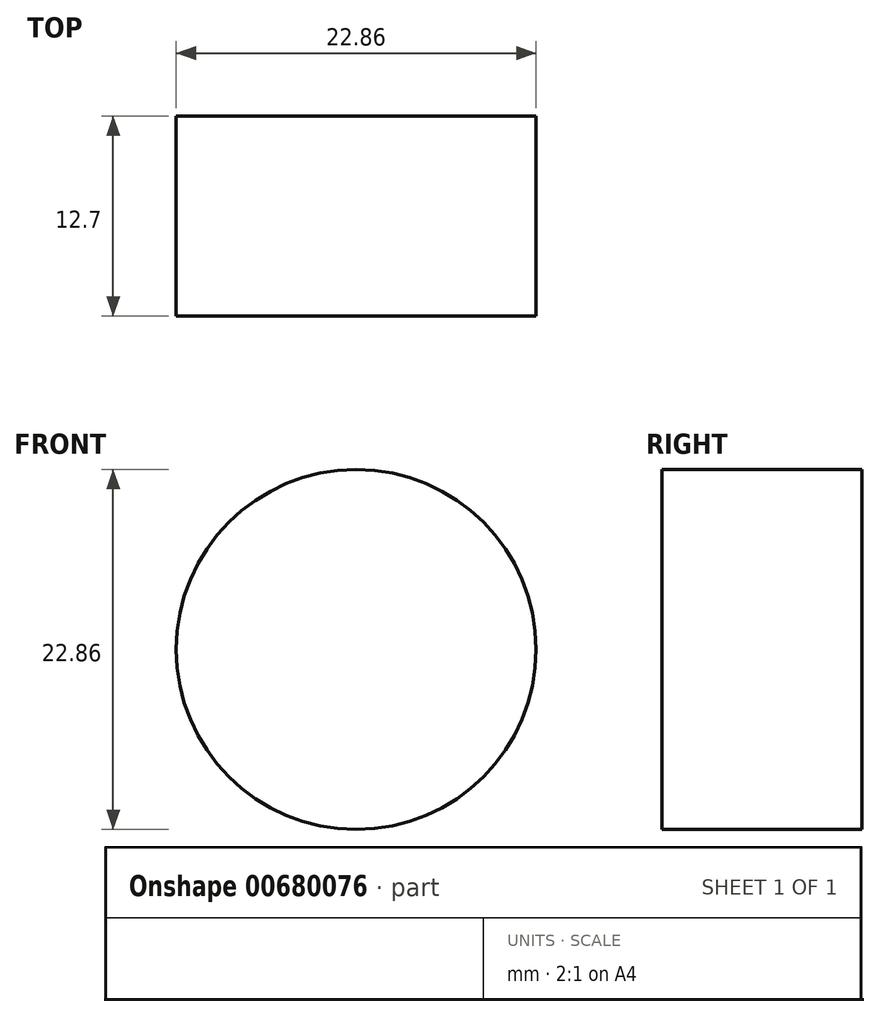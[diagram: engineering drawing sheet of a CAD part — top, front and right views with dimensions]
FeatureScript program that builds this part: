
annotation { "Feature Type Name" : "Feature", "Feature Type Description" : "" }
export const myFeature = defineFeature(function(context is Context, id is Id, definition is map)
    precondition{}
    {
        {
            var Q0;
            Q0=qCreatedBy(makeId("Front.planeOp"),FACE);
            var sketch = newSketch(context, id + "F0", { "sketchPlane" : qUnion([Q0])});
            skCircle(sketch, "E0", {"center": v(0, 0) * mm, "radius": 11.43 * mm});
            skSolve(sketch);
        }
        {
            var Q0;
            Q0=makeQuery(id+"F0.imprint","IMPRINT",FACE,{"disambiguationData":[TD([[makeQuery(id+"F0.imprint","IMPRINT",EDGE,{"derivedFrom":sQuery(id+"F0.wireOp",EDGE,"E0")}),1.0]])]});
            extrude(context, id + "F1", {"entities" : qUnion([Q0]), "depth" : 12.7 * mm, "offsetDistance" : 25.4 * mm});
        }
    });
